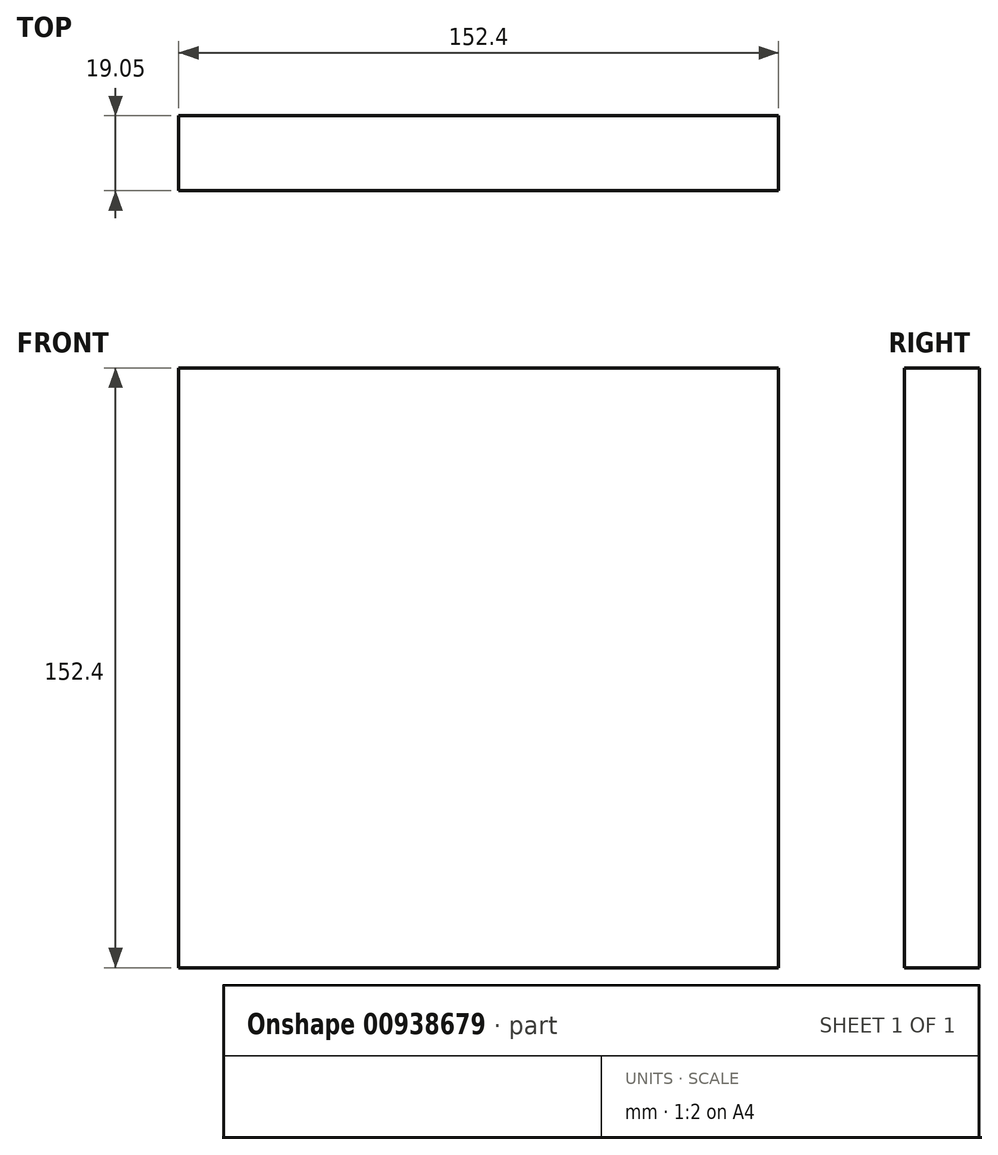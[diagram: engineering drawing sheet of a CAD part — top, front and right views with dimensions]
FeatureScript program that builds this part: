
annotation { "Feature Type Name" : "Feature", "Feature Type Description" : "" }
export const myFeature = defineFeature(function(context is Context, id is Id, definition is map)
    precondition{}
    {
        {
            var Q0;
            Q0=qCreatedBy(makeId("Front.planeOp"),FACE);
            var sketch = newSketch(context, id + "F0", { "sketchPlane" : qUnion([Q0])});
            skLineSegment(sketch, "E0.bottom", {"start": v(76.2, -76.2) * mm, "end": v(-76.2, -76.2) * mm});
            skLineSegment(sketch, "E0.top", {"start": v(76.2, 76.2) * mm, "end": v(-76.2, 76.2) * mm});
            skLineSegment(sketch, "E0.left", {"start": v(76.2, -76.2) * mm, "end": v(76.2, 76.2) * mm});
            skLineSegment(sketch, "E0.right", {"start": v(-76.2, -76.2) * mm, "end": v(-76.2, 76.2) * mm});
            skPoint(sketch, "E0.middle", {"position": v(0, 0) * mm});
            skSolve(sketch);
        }
        {
            var Q0;
            Q0=qSketchRegion(id+"F0",true);
            extrude(context, id + "F1", {"entities" : qUnion([Q0]), "depth" : 19.05 * mm, "offsetDistance" : 25.4 * mm});
        }
    });
